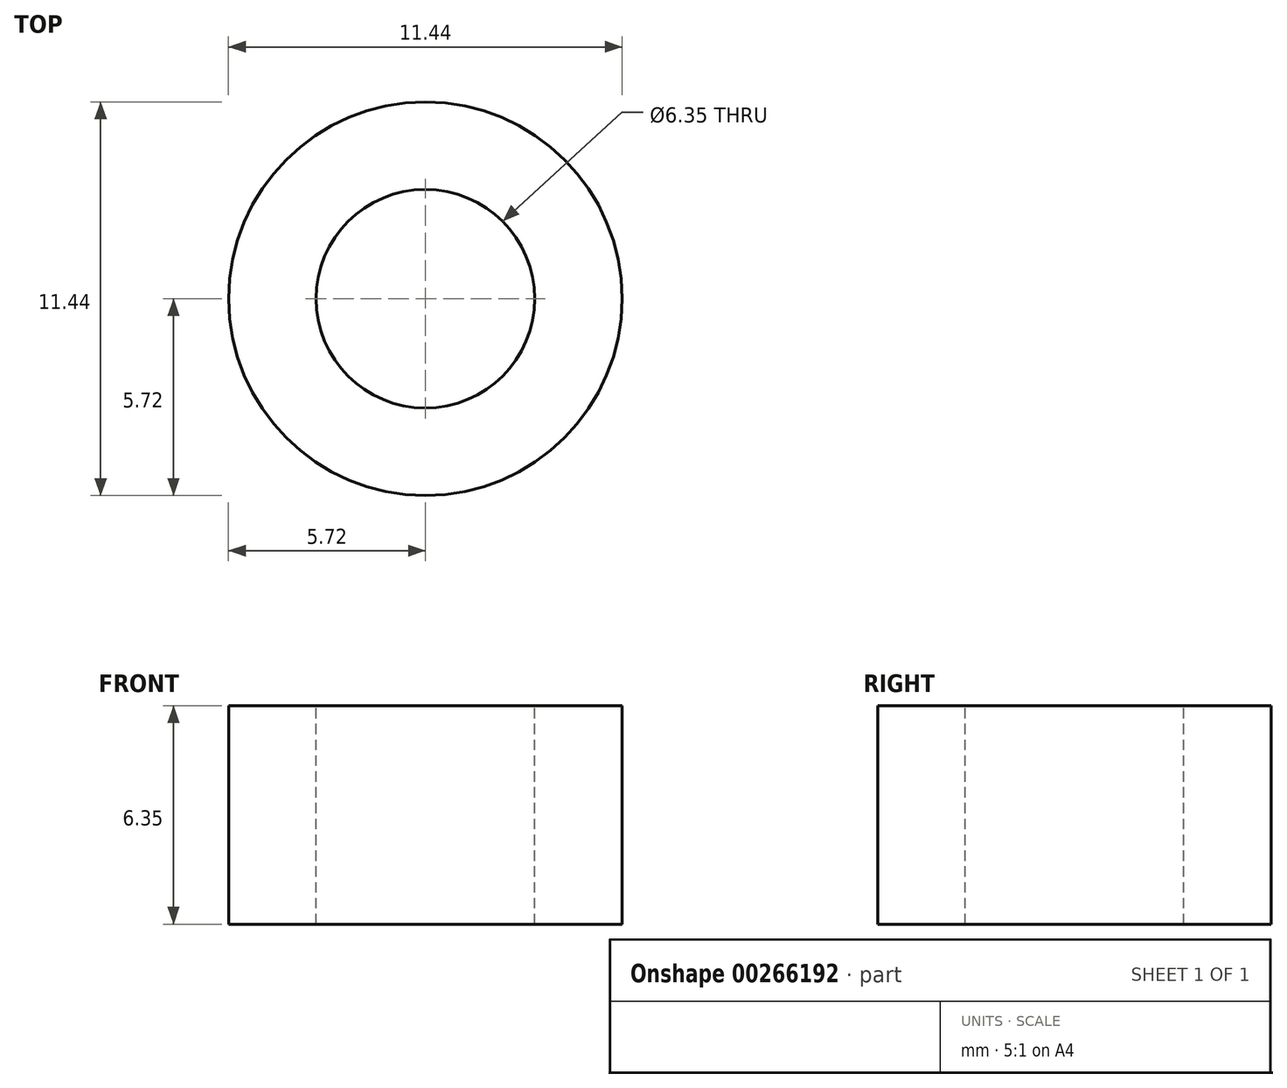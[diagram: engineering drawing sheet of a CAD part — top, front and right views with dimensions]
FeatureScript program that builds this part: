
annotation { "Feature Type Name" : "Feature", "Feature Type Description" : "" }
export const myFeature = defineFeature(function(context is Context, id is Id, definition is map)
    precondition{}
    {
        {
            var Q0;
            Q0=qCreatedBy(makeId("Front.planeOp"),FACE);
            var sketch = newSketch(context, id + "F0", { "sketchPlane" : qUnion([Q0])});
            skLineSegment(sketch, "E0", {"start": v(0, 0) * mm, "end": v(0, 6.35) * mm});
            skLineSegment(sketch, "E1", {"start": v(0, 6.35) * mm, "end": v(5.72, 6.35) * mm});
            skLineSegment(sketch, "E2", {"start": v(5.72, 6.35) * mm, "end": v(5.72, 0) * mm});
            skLineSegment(sketch, "E3", {"start": v(5.72, 0) * mm, "end": v(0, 0) * mm});
            skSolve(sketch);
        }
        {
            var Q0;
            Q0=makeQuery(id+"F0.imprint","IMPRINT",FACE,{"disambiguationData":[TD([[makeQuery(id+"F0.imprint","IMPRINT",EDGE,{"derivedFrom":sQuery(id+"F0.wireOp",EDGE,"E0")}),-1.0]])]});
            var Q1;
            Q1=sQuery(id+"F0.wireOp",EDGE,"E0");
            revolve(context, id + "F1", {"entities" : qUnion([Q0]), "axis" : qUnion([Q1]), "revolveType" : RevolveType.FULL});
        }
        {
            var Q0;
            Q0=makeQuery(id+"F1.opRevolve","SWEPT_FACE",FACE,{"disambiguationData":[OSD([sQuery(id+"F0.wireOp",EDGE,"E1")])]});
            var sketch = newSketch(context, id + "F2", { "sketchPlane" : qUnion([Q0])});
            skPoint(sketch, "E4", {"position": v(0, 0) * mm});
            skSolve(sketch);
        }
        {
            var Q0;
            Q0=sQuery(id+"F2.wireOp",VERTEX,"E4");
            var Q1;
            Q1=makeQuery(id+"F1.opRevolve","SWEPT_BODY",BODY,{"disambiguationData":[OSD([sQuery(id+"F0.wireOp",EDGE,"E0"),sQuery(id+"F0.wireOp",EDGE,"E1"),sQuery(id+"F0.wireOp",EDGE,"E2"),sQuery(id+"F0.wireOp",EDGE,"E3")])]});
            hole(context, id + "F3", {"style" : HoleStyle.SIMPLE, "endStyle" : HoleEndStyle.THROUGH, "holeDiameter" : 6.35 * mm, "tappedDepth" : 12.7 * mm, "tapClearance" : 3, "locations" : qUnion([Q0]), "scope" : qUnion([Q1])});
        }
    });
